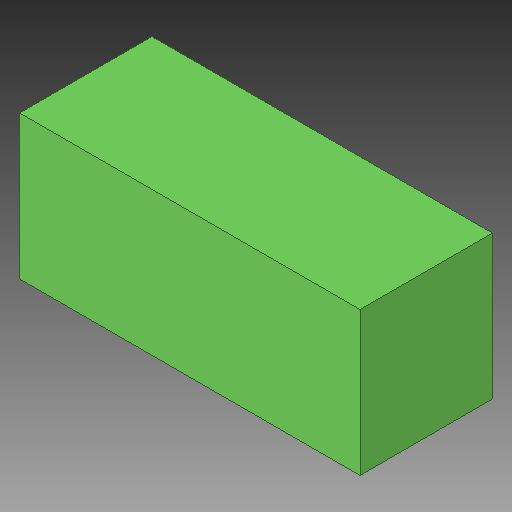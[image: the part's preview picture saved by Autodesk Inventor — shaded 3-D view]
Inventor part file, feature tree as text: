
AUTODESK INVENTOR PART (.ipt)
format: ipt  version: 2019.2 (Build 232265000, 265)  size: 100,864 bytes
history: native  units: mm
features: extrude x1, fillet x1, sketch x1
ambient origin geometry x8: Origin, YZ Plane, XZ Plane, XY Plane, X Axis, Y Axis, Z Axis, Center Point
bodies: Solid1 (feature_tree)
feature tree (3):
  extrude  "Extrusion1"  Depth=76.0mm
  fillet  "Fillet1"  Radius=70.0mm
  sketch  "Sketch1"  dims[d0=180.0mm d1=76.0mm d2=70.0mm d3=0.0mm d4=2.0mm]
